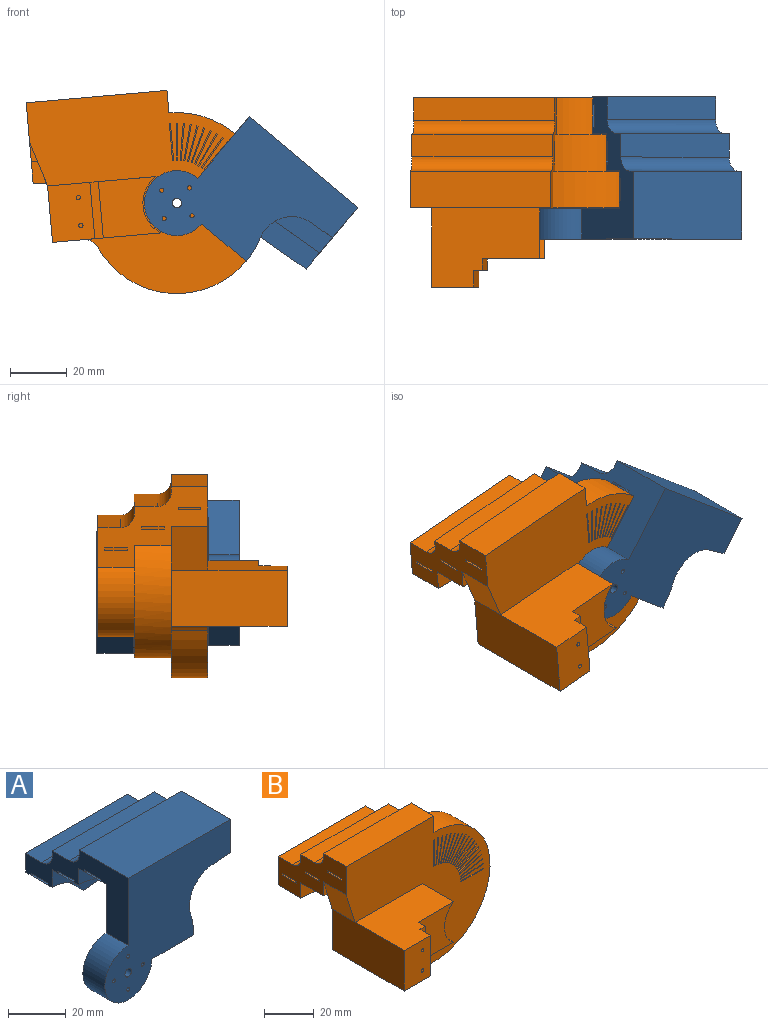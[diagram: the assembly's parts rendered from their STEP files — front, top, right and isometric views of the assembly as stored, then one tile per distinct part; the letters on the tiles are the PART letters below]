
ASSEMBLY  parts=2 mates=1
PART A: 42 faces, bbox 61.5x50.3x51.5 mm
  f0: plane 50.3x28.5mm, normal (-1,0,0), area 611.2mm2, adj f2,f3,f5,f8,f9,f11,f12,f15
  f1: plane 50.3x28.5mm, normal (1,0,0), area 695.7mm2, adj f3,f4,f5,f6,f8,f9,f10,f11
  f2: plane 27.05x15.58mm, normal (0,-1,0), area 187.8mm2, adj f0,f4,f16,f25
  f3: plane 50x2.5mm, normal (0,1,0), area 125mm2, adj f0,f1,f15,f38
  f4: plane 31.15x13.3mm, normal (0.08,0,-1), area 413.2mm2, adj f1,f2,f14,f16,f22,f25
  f5: plane 50x2mm, normal (0,1,0), area 100mm2, adj f0,f1,f8,f39
  f6: plane 28.44x24mm, normal (0.08,0,-1), area 476.7mm2, adj f1,f14,f16,f17,f37,f40
  f7: cylinder r=32mm len=10.7mm, axis (0,1,0), area 105.1mm2, adj f13,f17,f37,f40
  f8: plane 50x24mm, normal (0,0,1), area 1200mm2, adj f0,f1,f5,f40
  f9: plane 50x0.8mm, normal (0,-1,0), area 40mm2, adj f0,f1,f10,f12
  f10: plane 50x8mm, normal (0,0,1), area 400mm2, adj f1,f9,f11,f16
  f11: plane 50x0.8mm, normal (0,1,0), area 40mm2, adj f0,f1,f10,f12
  f12: plane 50x8mm, normal (0,0,-1), area 400mm2, adj f0,f1,f9,f11
  f13: plane 20.5x10.7mm, normal (0,0,-1), area 219.4mm2, adj f7,f17,f31,f40
  f14: plane 28.44x8.9mm, normal (0,-1,0), area 178.2mm2, adj f1,f4,f6,f16
  f15: plane 50x8.3mm, normal (0,0,1), area 415mm2, adj f0,f1,f3,f39
  f16: cylinder r=32mm len=27.05mm, axis (0,1,0), area 324.3mm2, adj f0,f2,f4,f6,f10,f14,f17
  f17: plane 52.45x43.5mm, normal (0,1,0), area 1171.8mm2, adj f0,f6,f7,f13,f16,f31,f32,f33
  f18: plane 50x0.8mm, normal (0,-1,0), area 40mm2, adj f0,f1,f19,f21
  f19: plane 50x8mm, normal (0,0,1), area 400mm2, adj f1,f18,f20,f25
  f20: plane 50x0.8mm, normal (0,1,0), area 40mm2, adj f0,f1,f19,f21
  f21: plane 50x8mm, normal (0,0,-1), area 400mm2, adj f0,f1,f18,f20
  f22: plane 50x16.38mm, normal (0,-1,0), area 396.3mm2, adj f0,f1,f4,f23,f25,f26
  f23: plane 34.77x13mm, normal (0.08,0,-1), area 453.6mm2, adj f1,f22,f26,f41
  f24: plane 50x8mm, normal (0,0,1), area 400mm2, adj f0,f1,f38,f41
  f25: cylinder r=25mm len=18.85mm, axis (0,1,0), area 277.6mm2, adj f0,f2,f4,f19,f22
  f26: cylinder r=17.5mm len=15.23mm, axis (0,-1,0), area 240.2mm2, adj f0,f22,f23,f28,f41
  f27: plane 50x0.8mm, normal (0,-1,0), area 40mm2, adj f0,f1,f28,f30
  f28: plane 50x8mm, normal (0,0,1), area 400mm2, adj f1,f26,f27,f29
  f29: plane 50x0.8mm, normal (0,1,0), area 40mm2, adj f0,f1,f28,f30
  f30: plane 50x8mm, normal (0,0,-1), area 400mm2, adj f0,f1,f27,f29
  f31: cylinder r=11.5mm len=23mm, axis (0,-1,0), area 579.9mm2, adj f0,f13,f17,f40
  f32: cylinder r=0.75mm len=10.7mm, axis (0,-1,0), area 50.4mm2, adj f17,f40
  f33: cylinder r=0.75mm len=10.7mm, axis (0,-1,0), area 50.4mm2, adj f17,f40
  f34: cylinder r=0.75mm len=10.7mm, axis (0,-1,0), area 50.4mm2, adj f17,f40
  f35: cylinder r=0.75mm len=10.7mm, axis (0,-1,0), area 50.4mm2, adj f17,f40
  f36: cylinder r=1.65mm len=10.7mm, axis (0,-1,0), area 110.9mm2, adj f17,f40
  f37: cylinder r=12mm len=15.58mm, axis (0,1,0), area 230.5mm2, adj f6,f7,f17,f40
  f38: cylinder r=5mm len=50mm, axis (1,0,0), area 392.7mm2, adj f0,f1,f3,f24
  f39: cylinder r=5mm len=50mm, axis (1,0,0), area 392.7mm2, adj f0,f1,f5,f15
  f40: plane 61.5x51.5mm, normal (0,-1,0), area 1832.4mm2, adj f0,f1,f6,f7,f8,f13,f31,f32
  f41: plane 50x16.88mm, normal (0,1,0), area 697.9mm2, adj f0,f1,f23,f24,f26
PART B: 153 faces, bbox 82x67x72 mm
  f0: cylinder r=32mm len=64mm, axis (0,1,0), area 1786.7mm2, adj f6,f8,f10,f14,f150
  f1: cylinder r=1.65mm len=15mm, axis (0,-1,0), area 155.5mm2, adj f6,f140
  f2: plane 20x15mm, normal (0,-1,0), area 296.5mm2, adj f3,f5,f130,f131,f135,f137
  f3: plane 41x38.37mm, normal (0,0,-1), area 997.9mm2, adj f2,f4,f6,f10,f130,f131,f132,f133
  f4: cylinder r=12mm len=20mm, axis (0,1,0), area 425.6mm2, adj f3,f5,f6,f134
  f5: plane 38.37x28mm, normal (0,0,1), area 852.6mm2, adj f2,f4,f6,f130,f131,f132,f133,f134
  f6: plane 82x72mm, normal (0,-1,0), area 3660.9mm2, adj f0,f1,f3,f4,f5,f7,f8,f13
  f7: plane 39x28.5mm, normal (-1,0,0), area 537.5mm2, adj f6,f9,f12,f13,f14,f15,f16,f17
  f8: plane 39x22.5mm, normal (1,0,0), area 303.5mm2, adj f0,f6,f9,f10,f11,f12,f13,f15
  f9: plane 50x2.5mm, normal (0,1,0), area 125mm2, adj f7,f8,f118,f151
  f10: plane 79.75x64mm, normal (0,1,0), area 1477.8mm2, adj f0,f3,f8,f11,f117,f130,f149,f150
  f11: cylinder r=25mm len=50mm, axis (0,-1,0), area 1764.4mm2, adj f8,f10,f113,f117,f119,f123
  f12: plane 50x2mm, normal (0,1,0), area 100mm2, adj f7,f8,f13,f152
  f13: plane 50x13mm, normal (0,0,1), area 650mm2, adj f6,f7,f8,f12
  f14: plane 50x8mm, normal (0,0,1), area 400mm2, adj f0,f7,f15,f17
  f15: plane 50x0.8mm, normal (0,-1,0), area 40mm2, adj f7,f8,f14,f16
  f16: plane 50x8mm, normal (0,0,-1), area 400mm2, adj f7,f8,f15,f17
  f17: plane 50x0.8mm, normal (0,1,0), area 40mm2, adj f7,f8,f14,f16
  f18: plane 3x0.33mm, normal (0.82,0,0.57), area 1.2mm2, adj f6,f19,f21,f22
  f19: plane 10.65x7.46mm, normal (-0.57,0,0.82), area 39mm2, adj f6,f18,f20,f22
  f20: plane 3x0.33mm, normal (-0.82,0,-0.57), area 1.2mm2, adj f6,f19,f21,f22
  f21: plane 10.65x7.46mm, normal (0.57,0,-0.82), area 39mm2, adj f6,f18,f20,f22
  f22: plane 10.88x7.78mm, normal (0,-1,0), area 5.2mm2, adj f18,f19,f20,f21
  f23: plane 3x0.35mm, normal (0.87,0,0.5), area 1.2mm2, adj f6,f24,f26,f27
  f24: plane 11.26x6.5mm, normal (-0.5,0,0.87), area 39mm2, adj f6,f23,f25,f27
  f25: plane 3x0.35mm, normal (-0.87,0,-0.5), area 1.2mm2, adj f6,f24,f26,f27
  f26: plane 11.26x6.5mm, normal (0.5,0,-0.87), area 39mm2, adj f6,f23,f25,f27
  f27: plane 11.46x6.85mm, normal (0,-1,0), area 5.2mm2, adj f23,f24,f25,f26
  f28: plane 3x0.28mm, normal (0.71,0,0.71), area 1.2mm2, adj f6,f29,f31,f32
  f29: plane 9.19x9.19mm, normal (-0.71,0,0.71), area 39mm2, adj f6,f28,f30,f32
  f30: plane 3x0.28mm, normal (-0.71,0,-0.71), area 1.2mm2, adj f6,f29,f31,f32
  f31: plane 9.19x9.19mm, normal (0.71,0,-0.71), area 39mm2, adj f6,f28,f30,f32
  f32: plane 9.48x9.48mm, normal (0,-1,0), area 5.2mm2, adj f28,f29,f30,f31
  f33: plane 3x0.31mm, normal (0.77,0,0.64), area 1.2mm2, adj f6,f34,f36,f37
  f34: plane 9.96x8.36mm, normal (-0.64,0,0.77), area 39mm2, adj f6,f33,f35,f37
  f35: plane 3x0.31mm, normal (-0.77,0,-0.64), area 1.2mm2, adj f6,f34,f36,f37
  f36: plane 9.96x8.36mm, normal (0.64,0,-0.77), area 39mm2, adj f6,f33,f35,f37
  f37: plane 10.22x8.66mm, normal (0,-1,0), area 5.2mm2, adj f33,f34,f35,f36
  f38: plane 3x0.39mm, normal (0.97,0,0.26), area 1.2mm2, adj f6,f39,f41,f42
  f39: plane 12.56x3.36mm, normal (-0.26,0,0.97), area 39mm2, adj f6,f38,f40,f42
  f40: plane 3x0.39mm, normal (-0.97,0,-0.26), area 1.2mm2, adj f6,f39,f41,f42
  f41: plane 12.56x3.36mm, normal (0.26,0,-0.97), area 39mm2, adj f6,f38,f40,f42
  f42: plane 12.66x3.75mm, normal (0,-1,0), area 5.2mm2, adj f38,f39,f40,f41
  f43: plane 3x0.39mm, normal (0.98,0,0.17), area 1.2mm2, adj f6,f44,f46,f47
  f44: plane 12.8x3mm, normal (-0.17,0,0.98), area 39mm2, adj f6,f43,f45,f47
  f45: plane 3x0.39mm, normal (-0.98,0,-0.17), area 1.2mm2, adj f6,f44,f46,f47
  f46: plane 12.8x3mm, normal (0.17,0,-0.98), area 39mm2, adj f6,f43,f45,f47
  f47: plane 12.87x2.65mm, normal (0,-1,0), area 5.2mm2, adj f43,f44,f45,f46
  f48: plane 3x0.36mm, normal (0.91,0,0.42), area 1.2mm2, adj f6,f49,f51,f52
  f49: plane 11.78x5.49mm, normal (-0.42,0,0.91), area 39mm2, adj f6,f48,f50,f52
  f50: plane 3x0.36mm, normal (-0.91,0,-0.42), area 1.2mm2, adj f6,f49,f51,f52
  f51: plane 11.78x5.49mm, normal (0.42,0,-0.91), area 39mm2, adj f6,f48,f50,f52
  f52: plane 11.95x5.86mm, normal (0,-1,0), area 5.2mm2, adj f48,f49,f50,f51
  f53: plane 3x0.38mm, normal (0.94,0,0.34), area 1.2mm2, adj f6,f54,f56,f57
  f54: plane 12.22x4.45mm, normal (-0.34,0,0.94), area 39mm2, adj f6,f53,f55,f57
  f55: plane 3x0.38mm, normal (-0.94,0,-0.34), area 1.2mm2, adj f6,f54,f56,f57
  f56: plane 12.22x4.45mm, normal (0.34,0,-0.94), area 39mm2, adj f6,f53,f55,f57
  f57: plane 12.35x4.82mm, normal (0,-1,0), area 5.2mm2, adj f53,f54,f55,f56
  f58: plane 3x0.39mm, normal (0.26,0,0.97), area 1.2mm2, adj f6,f59,f61,f62
  f59: plane 12.56x3.36mm, normal (-0.97,0,0.26), area 39mm2, adj f6,f58,f60,f62
  f60: plane 3x0.39mm, normal (-0.26,0,-0.97), area 1.2mm2, adj f6,f59,f61,f62
  f61: plane 12.56x3.36mm, normal (0.97,0,-0.26), area 39mm2, adj f6,f58,f60,f62
  f62: plane 12.66x3.75mm, normal (0,-1,0), area 5.2mm2, adj f58,f59,f60,f61
  f63: plane 3x0.38mm, normal (0.34,0,0.94), area 1.2mm2, adj f6,f64,f66,f67
  f64: plane 12.22x4.45mm, normal (-0.94,0,0.34), area 39mm2, adj f6,f63,f65,f67
  f65: plane 3x0.38mm, normal (-0.34,0,-0.94), area 1.2mm2, adj f6,f64,f66,f67
  f66: plane 12.22x4.45mm, normal (0.94,0,-0.34), area 39mm2, adj f6,f63,f65,f67
  f67: plane 12.35x4.82mm, normal (0,-1,0), area 5.2mm2, adj f63,f64,f65,f66
  f68: plane 3x0.4mm, normal (0.09,0,1), area 1.2mm2, adj f6,f69,f71,f72
  f69: plane 12.95x3mm, normal (-1,0,0.09), area 39mm2, adj f6,f68,f70,f72
  f70: plane 3x0.4mm, normal (-0.09,0,-1), area 1.2mm2, adj f6,f69,f71,f72
  f71: plane 12.95x3mm, normal (1,0,-0.09), area 39mm2, adj f6,f68,f70,f72
  f72: plane 12.99x1.53mm, normal (0,-1,0), area 5.2mm2, adj f68,f69,f70,f71
  f73: plane 3x0.39mm, normal (0.17,0,0.98), area 1.2mm2, adj f6,f74,f76,f77
  f74: plane 12.8x3mm, normal (-0.98,0,0.17), area 39mm2, adj f6,f73,f75,f77
  f75: plane 3x0.39mm, normal (-0.17,0,-0.98), area 1.2mm2, adj f6,f74,f76,f77
  f76: plane 12.8x3mm, normal (0.98,0,-0.17), area 39mm2, adj f6,f73,f75,f77
  f77: plane 12.87x2.65mm, normal (0,-1,0), area 5.2mm2, adj f73,f74,f75,f76
  f78: plane 3x0.33mm, normal (0.57,0,0.82), area 1.2mm2, adj f6,f79,f81,f82
  f79: plane 10.65x7.46mm, normal (-0.82,0,0.57), area 39mm2, adj f6,f78,f80,f82
  f80: plane 3x0.33mm, normal (-0.57,0,-0.82), area 1.2mm2, adj f6,f79,f81,f82
  f81: plane 10.65x7.46mm, normal (0.82,0,-0.57), area 39mm2, adj f6,f78,f80,f82
  f82: plane 10.88x7.78mm, normal (0,-1,0), area 5.2mm2, adj f78,f79,f80,f81
  f83: plane 3x0.31mm, normal (0.64,0,0.77), area 1.2mm2, adj f6,f84,f86,f87
  f84: plane 9.96x8.36mm, normal (-0.77,0,0.64), area 39mm2, adj f6,f83,f85,f87
  f85: plane 3x0.31mm, normal (-0.64,0,-0.77), area 1.2mm2, adj f6,f84,f86,f87
  f86: plane 9.96x8.36mm, normal (0.77,0,-0.64), area 39mm2, adj f6,f83,f85,f87
  f87: plane 10.22x8.66mm, normal (0,-1,0), area 5.2mm2, adj f83,f84,f85,f86
  f88: plane 3x0.36mm, normal (0.42,0,0.91), area 1.2mm2, adj f6,f89,f91,f92
  f89: plane 11.78x5.49mm, normal (-0.91,0,0.42), area 39mm2, adj f6,f88,f90,f92
  f90: plane 3x0.36mm, normal (-0.42,0,-0.91), area 1.2mm2, adj f6,f89,f91,f92
  f91: plane 11.78x5.49mm, normal (0.91,0,-0.42), area 39mm2, adj f6,f88,f90,f92
  f92: plane 11.95x5.86mm, normal (0,-1,0), area 5.2mm2, adj f88,f89,f90,f91
  f93: plane 3x0.35mm, normal (0.5,0,0.87), area 1.2mm2, adj f6,f94,f96,f97
  f94: plane 11.26x6.5mm, normal (-0.87,0,0.5), area 39mm2, adj f6,f93,f95,f97
  f95: plane 3x0.35mm, normal (-0.5,0,-0.87), area 1.2mm2, adj f6,f94,f96,f97
  f96: plane 11.26x6.5mm, normal (0.87,0,-0.5), area 39mm2, adj f6,f93,f95,f97
  f97: plane 11.46x6.85mm, normal (0,-1,0), area 5.2mm2, adj f93,f94,f95,f96
  f98: plane 3x0.4mm, normal (1,0,0.09), area 1.2mm2, adj f6,f99,f101,f102
  f99: plane 12.95x3mm, normal (-0.09,0,1), area 39mm2, adj f6,f98,f100,f102
  f100: plane 3x0.4mm, normal (-1,0,-0.09), area 1.2mm2, adj f6,f99,f101,f102
  f101: plane 12.95x3mm, normal (0.09,0,-1), area 39mm2, adj f6,f98,f100,f102
  f102: plane 12.99x1.53mm, normal (0,-1,0), area 5.2mm2, adj f98,f99,f100,f101
  f103: plane 3x0.4mm, normal (1,0,0), area 1.2mm2, adj f6,f104,f106,f107
  f104: plane 13x3mm, normal (0,0,1), area 39mm2, adj f6,f103,f105,f107
  f105: plane 3x0.4mm, normal (-1,0,0), area 1.2mm2, adj f6,f104,f106,f107
  f106: plane 13x3mm, normal (0,0,-1), area 39mm2, adj f6,f103,f105,f107
  f107: plane 13x0.4mm, normal (0,-1,0), area 5.2mm2, adj f103,f104,f105,f106
  f108: plane 3x0.4mm, normal (0,0,-1), area 1.2mm2, adj f6,f109,f111,f112
  f109: plane 13x3mm, normal (1,0,0), area 39mm2, adj f6,f108,f110,f112
  f110: plane 3x0.4mm, normal (0,0,1), area 1.2mm2, adj f6,f109,f111,f112
  f111: plane 13x3mm, normal (-1,0,0), area 39mm2, adj f6,f108,f110,f112
  f112: plane 13x0.4mm, normal (0,-1,0), area 5.2mm2, adj f108,f109,f110,f111
  f113: plane 50x50mm, normal (0,1,0), area 820.4mm2, adj f8,f11,f114,f120
  f114: cylinder r=17.5mm len=35mm, axis (0,-1,0), area 1189.3mm2, adj f8,f113,f115,f120,f128
  f115: plane 67.5x43mm, normal (0,1,0), area 1244.5mm2, adj f7,f8,f114,f120,f121,f139
  f116: plane 7.19x2.25mm, normal (0,-1,0), area 7.9mm2, adj f7,f117,f149
  f117: plane 31.15x13mm, normal (-0.08,0,-1), area 406.3mm2, adj f7,f10,f11,f116,f119
  f118: plane 50x8mm, normal (0,0,1), area 400mm2, adj f7,f8,f9,f152
  f119: plane 31.15x9.72mm, normal (0,-1,0), area 215.3mm2, adj f7,f11,f117,f120
  f120: plane 34.77x13mm, normal (-0.08,0,-1), area 453.6mm2, adj f7,f113,f114,f115,f119
  f121: plane 50x8mm, normal (0,0,1), area 400mm2, adj f7,f8,f115,f151
  f122: plane 50x0.8mm, normal (0,1,0), area 40mm2, adj f7,f8,f123,f125
  f123: plane 50x8mm, normal (0,0,1), area 400mm2, adj f7,f11,f122,f124
  f124: plane 50x0.8mm, normal (0,-1,0), area 40mm2, adj f7,f8,f123,f125
  f125: plane 50x8mm, normal (0,0,-1), area 400mm2, adj f7,f8,f122,f124
  f126: plane 50x8mm, normal (0,0,-1), area 400mm2, adj f7,f8,f127,f129
  f127: plane 50x0.8mm, normal (0,1,0), area 40mm2, adj f7,f8,f126,f128
  f128: plane 50x8mm, normal (0,0,1), area 400mm2, adj f7,f114,f127,f129
  f129: plane 50x0.8mm, normal (0,-1,0), area 40mm2, adj f7,f8,f126,f128
  f130: plane 41x20mm, normal (-1,0,0), area 820mm2, adj f2,f3,f5,f10,f149
  f131: plane 20x6mm, normal (1,0,0), area 120mm2, adj f2,f3,f5,f132
  f132: plane 20x3mm, normal (0,-1,0), area 60mm2, adj f3,f5,f131,f133
  f133: plane 20x4mm, normal (1,0,0), area 80mm2, adj f3,f5,f132,f134
  f134: plane 20.37x20mm, normal (0,-1,0), area 331.8mm2, adj f3,f4,f5,f133
  f135: cylinder r=0.75mm len=6mm, axis (0,-1,0), area 28.3mm2, adj f2,f136
  f136: plane 1.5x1.5mm, normal (0,-1,0), area 1.8mm2, adj f135
  f137: cylinder r=0.75mm len=6mm, axis (0,-1,0), area 28.3mm2, adj f2,f138
  f138: plane 1.5x1.5mm, normal (0,-1,0), area 1.8mm2, adj f137
  f139: cylinder r=11.5mm len=24mm, axis (0,1,0), area 1734.2mm2, adj f115,f140
  f140: plane 23x23mm, normal (0,1,0), area 399.9mm2, adj f1,f139,f141,f143,f145,f147
  f141: cylinder r=0.75mm len=6mm, axis (0,1,0), area 28.3mm2, adj f140,f142
  f142: plane 1.5x1.5mm, normal (0,1,0), area 1.8mm2, adj f141
  f143: cylinder r=0.75mm len=6mm, axis (0,1,0), area 28.3mm2, adj f140,f144
  f144: plane 1.5x1.5mm, normal (0,1,0), area 1.8mm2, adj f143
  f145: cylinder r=0.75mm len=6mm, axis (0,1,0), area 28.3mm2, adj f140,f146
  f146: plane 1.5x1.5mm, normal (0,1,0), area 1.8mm2, adj f145
  f147: cylinder r=0.75mm len=6mm, axis (0,1,0), area 28.3mm2, adj f140,f148
  f148: plane 1.5x1.5mm, normal (0,1,0), area 1.8mm2, adj f147
  f149: plane 16x13mm, normal (-0.95,0,-0.3), area 217.9mm2, adj f6,f7,f10,f116,f130
  f150: cylinder r=5mm len=13mm, axis (0,1,0), area 75mm2, adj f0,f3,f6,f10
  f151: cylinder r=5mm len=50mm, axis (1,0,0), area 392.7mm2, adj f7,f8,f9,f121
  f152: cylinder r=5mm len=50mm, axis (1,0,0), area 392.7mm2, adj f7,f8,f12,f118
PLACE A rot(axis=(0,1,0),40deg) t=(4.63,-37.34,16.22)mm
PLACE B rot(axis=(0,-1,0),5deg) t=(-18.73,-30.84,23.59)mm
MATE cylindrical B.f0 <-> A.f16  axis (0,-1,0) through (-15.94,-28.84,-8.29)mm
